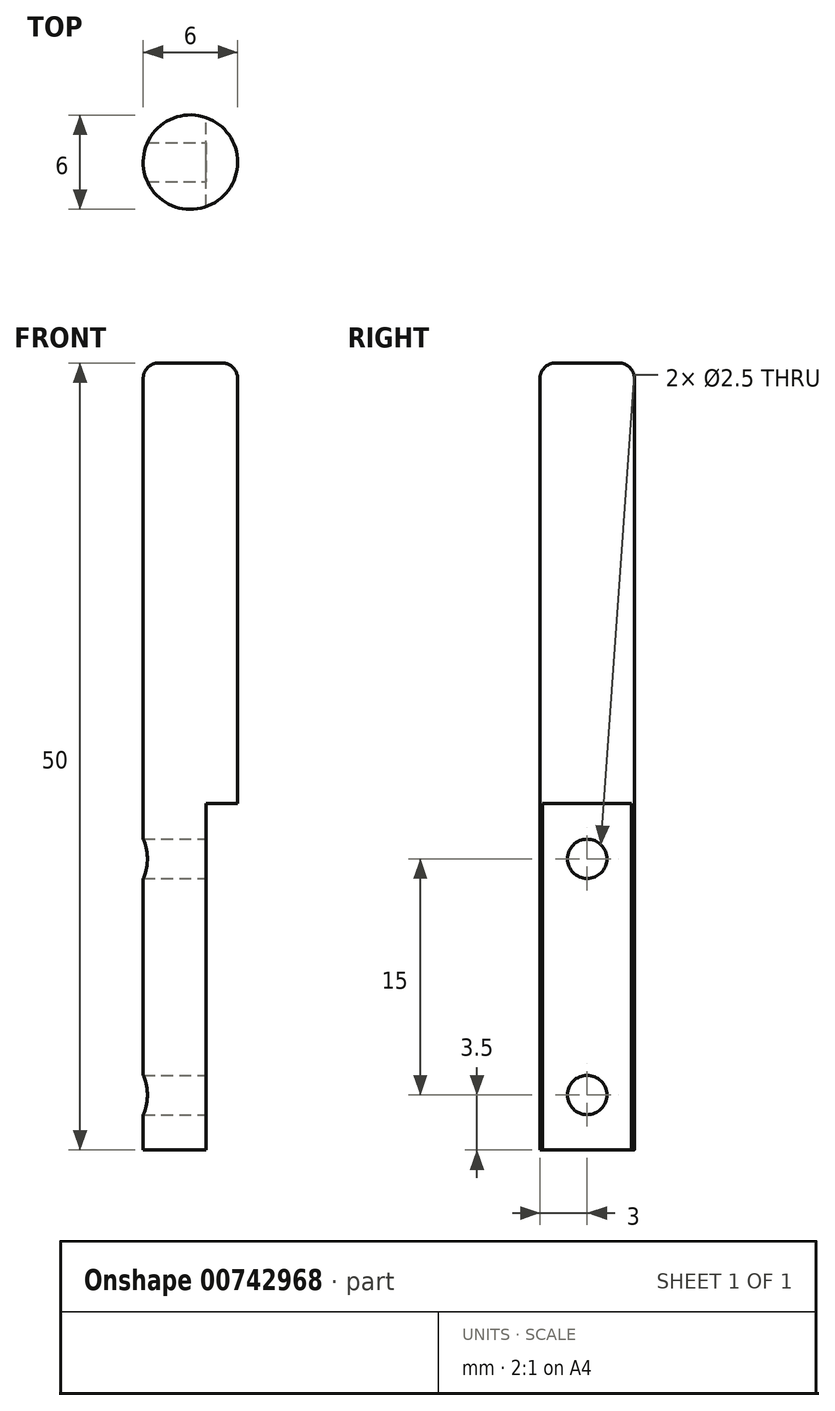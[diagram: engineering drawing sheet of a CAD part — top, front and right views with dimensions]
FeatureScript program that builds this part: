
annotation { "Feature Type Name" : "Feature", "Feature Type Description" : "" }
export const myFeature = defineFeature(function(context is Context, id is Id, definition is map)
    precondition{}
    {
        {
            var Q0;
            Q0=qCreatedBy(makeId("Top.planeOp"),FACE);
            var sketch = newSketch(context, id + "F0", { "sketchPlane" : qUnion([Q0])});
            skCircle(sketch, "E0", {"center": v(0, 0) * mm, "radius": 3 * mm});
            skSolve(sketch);
        }
        {
            var Q0;
            Q0=makeQuery(id+"F0.imprint","IMPRINT",FACE,{"disambiguationData":[TD([[makeQuery(id+"F0.imprint","IMPRINT",EDGE,{"derivedFrom":sQuery(id+"F0.wireOp",EDGE,"E0")}),1.0]])]});
            extrude(context, id + "F1", {"entities" : qUnion([Q0]), "depth" : 50 * mm, "offsetDistance" : 25 * mm});
        }
        {
            var Q0;
            Q0=makeQuery(id+"F1.opExtrude","CAP_EDGE",EDGE,{"disambiguationData":[OSD([sQuery(id+"F0.wireOp",EDGE,"E0")])],"isStart":false});
            fillet(context, id + "F2", {"entities" : qUnion([Q0]), "radius" : 1 * mm, "tangentPropagation" : true, "allowEdgeOverflow" : false});
        }
        {
            var Q0;
            Q0=qCreatedBy(makeId("Right.planeOp"),FACE);
            cPlane(context, id + "F3", {"entities" : qUnion([Q0]), "cplaneType" : CPlaneType.OFFSET, "offset" : 3 * mm, "width" : 150 * mm, "height" : 150 * mm});
        }
        {
            var Q0;
            Q0=qCreatedBy(id+"F3.planeOp",FACE);
            var sketch = newSketch(context, id + "F4", { "sketchPlane" : qUnion([Q0])});
            skLineSegment(sketch, "E1.bottom", {"start": v(-4.84, 22) * mm, "end": v(4.84, 22) * mm});
            skLineSegment(sketch, "E1.top", {"start": v(-4.84, -22) * mm, "end": v(4.84, -22) * mm});
            skLineSegment(sketch, "E1.left", {"start": v(-4.84, 22) * mm, "end": v(-4.84, -22) * mm});
            skLineSegment(sketch, "E1.right", {"start": v(4.84, 22) * mm, "end": v(4.84, -22) * mm});
            skPoint(sketch, "E1.middle", {"position": v(0, 0) * mm});
            skSolve(sketch);
        }
        {
            var Q0;
            Q0=makeQuery(id+"F4.imprint","IMPRINT",FACE,{"disambiguationData":[TD([[makeQuery(id+"F4.imprint","IMPRINT",EDGE,{"derivedFrom":sQuery(id+"F4.wireOp",EDGE,"E1.bottom")}),-1.0]])]});
            extrude(context, id + "F5", {"entities" : qUnion([Q0]), "operationType" : NewBodyOperationType.REMOVE, "oppositeDirection" : true, "depth" : 2 * mm, "offsetDistance" : 25 * mm});
        }
        {
            var Q0;
            Q0=makeQuery(id+"F5.boolean.opBoolean","COPY",FACE,{"derivedFrom":makeQuery(id+"F5.opExtrude","CAP_FACE",FACE,{"disambiguationData":[OSD([sQuery(id+"F4.wireOp",EDGE,"E1.bottom"),sQuery(id+"F4.wireOp",EDGE,"E1.top"),sQuery(id+"F4.wireOp",EDGE,"E1.left"),sQuery(id+"F4.wireOp",EDGE,"E1.right")])],"isStart":false})});
            var sketch = newSketch(context, id + "F6", { "sketchPlane" : qUnion([Q0])});
            skPoint(sketch, "E2", {"position": v(0, 3.5) * mm});
            skPoint(sketch, "E3", {"position": v(0, 18.5) * mm});
            skSolve(sketch);
        }
        {
            var Q0;
            Q0=sQuery(id+"F6.wireOp",VERTEX,"E2");
            var Q1;
            Q1=sQuery(id+"F6.wireOp",VERTEX,"E3");
            var Q2;
            Q2=makeQuery(id+"F1.opExtrude","SWEPT_BODY",BODY,{"disambiguationData":[OSD([sQuery(id+"F0.wireOp",EDGE,"E0")])]});
            hole(context, id + "F7", {"style" : HoleStyle.SIMPLE, "endStyle" : HoleEndStyle.THROUGH, "standardTappedOrClearance" : lookupTablePath({ "standard" : "ISO", "engagement" : "75%", "pitch" : "0.5 mm", "size" : "M3", "type" : "Tapped" }), "standardBlindInLast" : lookupTablePath({ "standard" : "ISO", "engagement" : "75%", "pitch" : "0.5 mm", "size" : "M3", "type" : "Tapped" }), "holeDiameter" : 2.5 * mm, "majorDiameter" : 3 * mm, "showTappedDepth" : true, "isTappedThrough" : true, "tappedDepth" : 13.25 * mm, "tapClearance" : 3, "locations" : qUnion([Q0, Q1]), "scope" : qUnion([Q2])});
        }
    });
